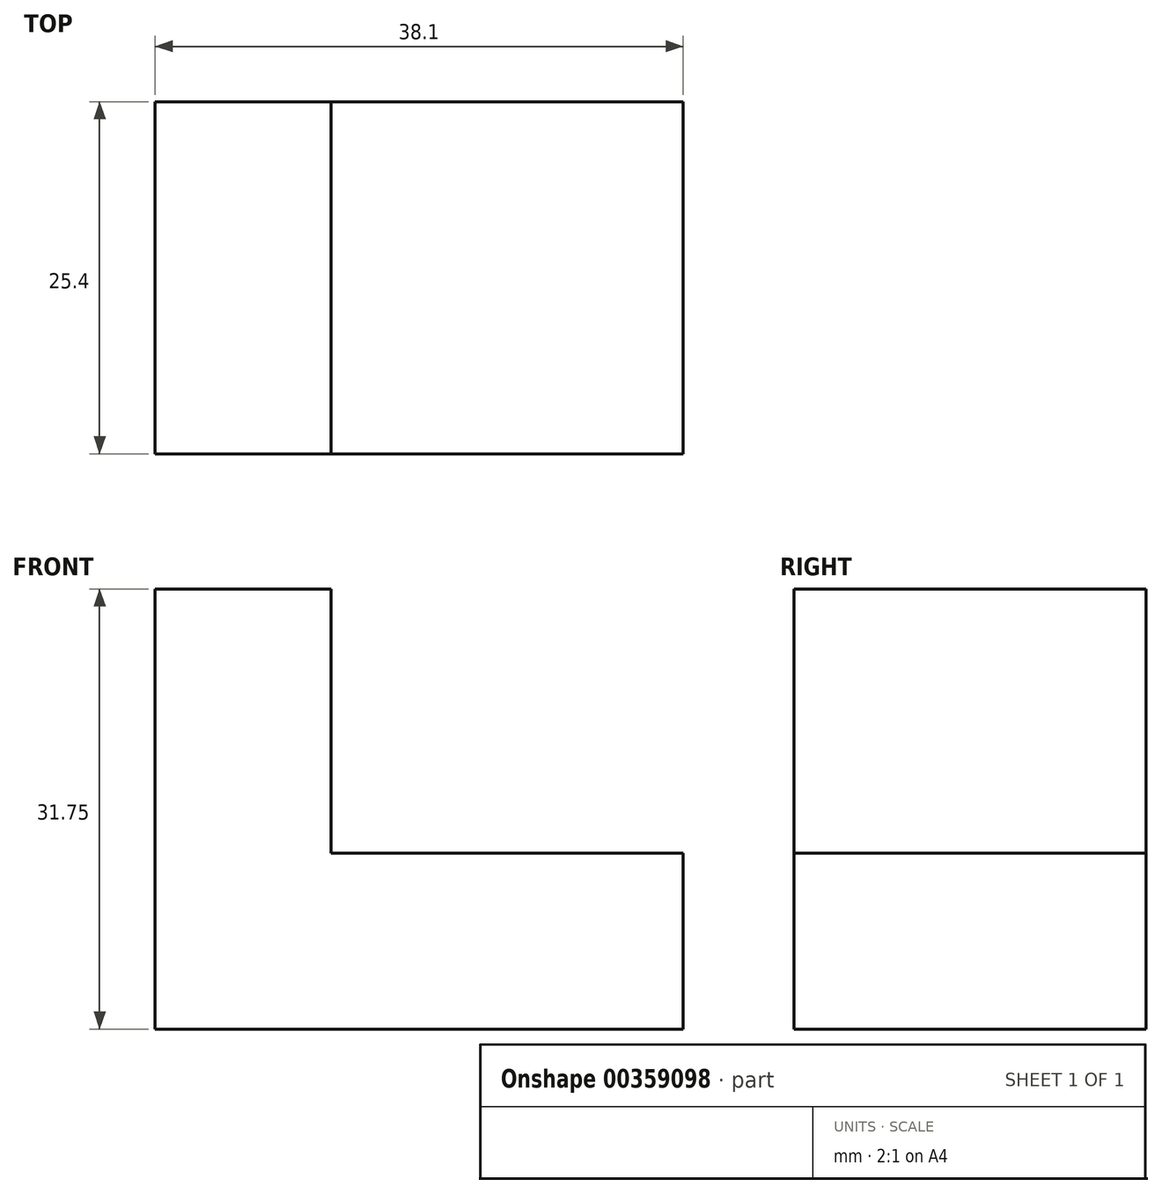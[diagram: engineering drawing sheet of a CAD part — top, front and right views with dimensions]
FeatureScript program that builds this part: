
annotation { "Feature Type Name" : "Feature", "Feature Type Description" : "" }
export const myFeature = defineFeature(function(context is Context, id is Id, definition is map)
    precondition{}
    {
        {
            var Q0;
            Q0=qCreatedBy(makeId("Front.planeOp"),FACE);
            var sketch = newSketch(context, id + "F0", { "sketchPlane" : qUnion([Q0])});
            skLineSegment(sketch, "E0", {"start": v(-28.1, 0) * mm, "end": v(-28.1, 31.75) * mm});
            skLineSegment(sketch, "E1", {"start": v(-28.1, 31.75) * mm, "end": v(-15.4, 31.75) * mm});
            skLineSegment(sketch, "E2", {"start": v(-15.4, 31.75) * mm, "end": v(-15.4, 12.7) * mm});
            skLineSegment(sketch, "E3", {"start": v(-15.4, 12.7) * mm, "end": v(10, 12.7) * mm});
            skLineSegment(sketch, "E4", {"start": v(10, 12.7) * mm, "end": v(10, 0) * mm});
            skLineSegment(sketch, "E5", {"start": v(10, 0) * mm, "end": v(-28.1, 0) * mm});
            skSolve(sketch);
        }
        {
            var Q0;
            Q0 = qSketchRegion(id + "F0", true);
            extrude(context, id + "F1", {"entities" : qUnion([Q0]), "depth" : 25.4 * mm});
        }
    });
